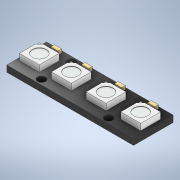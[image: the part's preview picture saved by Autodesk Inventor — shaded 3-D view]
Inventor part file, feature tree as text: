
AUTODESK INVENTOR PART (.ipt)
format: ipt  version: 2020.1 (Build 241239000, 239)  size: 253,440 bytes
history: native  units: mm
features: projected_geometry x7, extrude x6, sketch x3, plane x1
ambient origin geometry x8: Origin, YZ Plane, XZ Plane, XY Plane, X Axis, Y Axis, Z Axis, Center Point
bodies: Solid1 (feature_tree)
feature tree (17):
  sketch  "Sketch1"  dims[d0=31.84mm d1=10.0mm]
  extrude  "Extrusion1"  Depth=10.0mm
  extrude  "Extrusion2"  Depth=1.0mm
  extrude  "Extrusion3"  Depth=7.5mm
  sketch  "Sketch2"  dims[d2=1.85mm d3=1.0mm]
  extrude  "Extrusion4"  Depth=2.0mm
  extrude  "Extrusion5"  Depth=3.2mm
  plane  "Work Plane1"
  extrude  "Extrusion7"  Depth=0.5mm
  projected_geometry  "Projected Loop1"
  projected_geometry  "Projected Loop2"
  projected_geometry  "Projected Loop3"
  projected_geometry  "Projected Loop4"
  sketch  "Sketch3"  dims[d4=7.5mm d5=7.5mm d6=2.0mm d7=3.2mm d8=0.5mm d9=5.0mm d10=0.7mm d11=3.7mm d12=0.7mm d14=6.45mm d15=6.45mm d16=2.5mm d18=3.7mm d19=1.6mm d20=0.0mm d21=1.6mm d22=0.0mm d23=0.9mm d24=0.0mm d25=3.5mm d26=45.0deg d27=1.0mm d28=0.2mm d29=0.0mm d30=0.8mm d31=0.0mm d34=-0.1mm d35=10.0mm d36=0.0mm]
  projected_geometry  "Projected Loop5"
  projected_geometry  "Projected Loop6"
  projected_geometry  "Projected Loop7"
